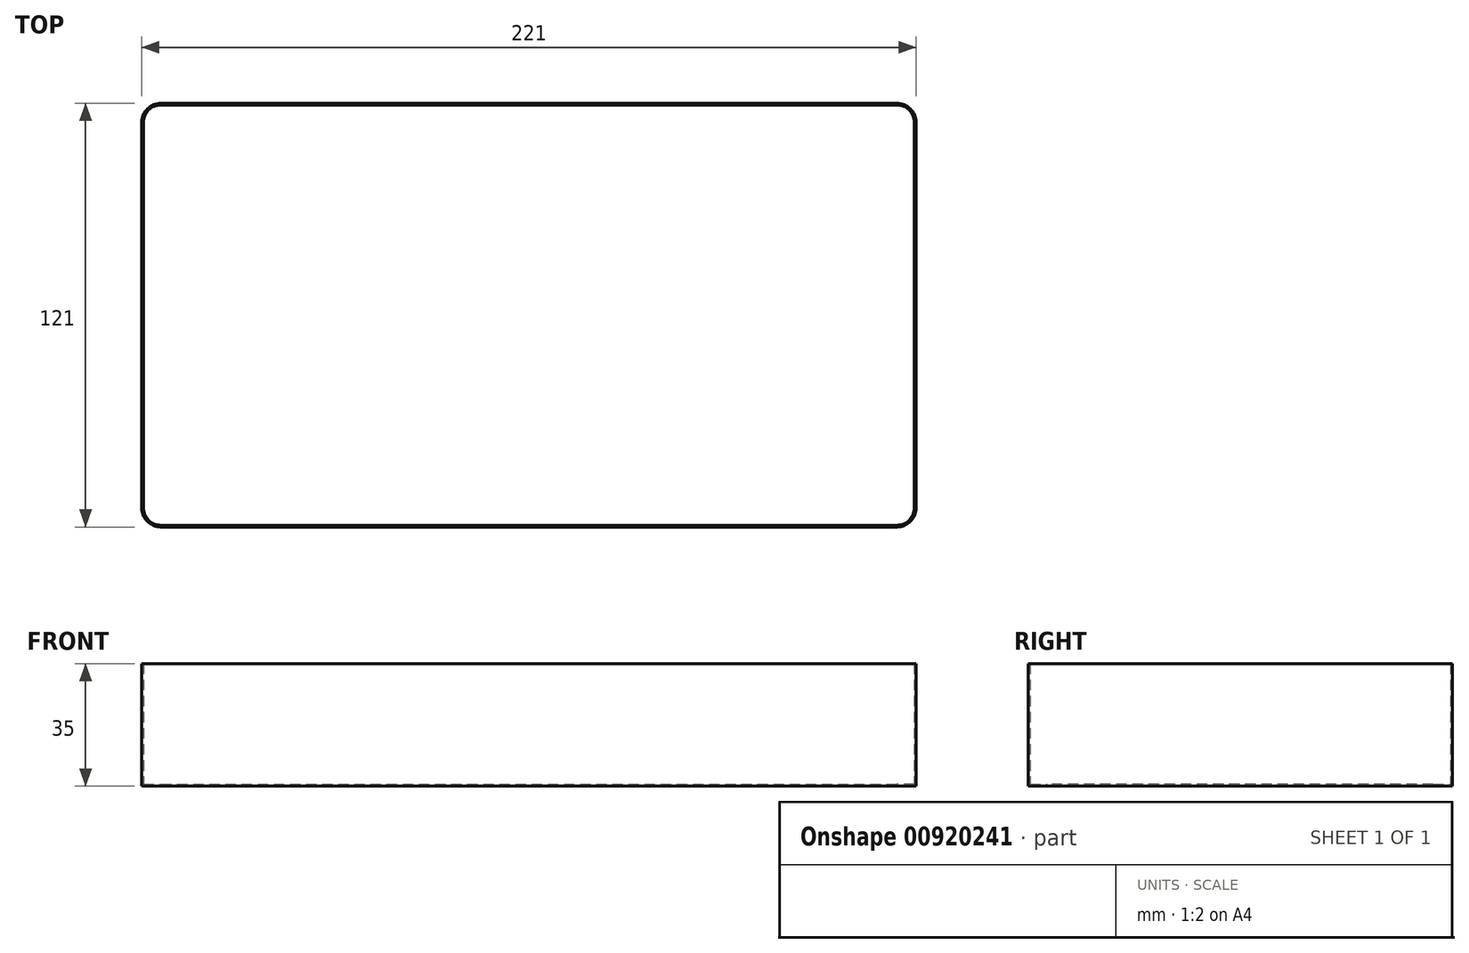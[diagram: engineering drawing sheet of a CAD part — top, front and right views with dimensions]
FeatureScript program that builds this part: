
annotation { "Feature Type Name" : "Feature", "Feature Type Description" : "" }
export const myFeature = defineFeature(function(context is Context, id is Id, definition is map)
    precondition{}
    {
        {
            var Q0;
            Q0=qCreatedBy(makeId("Top.planeOp"),FACE);
            var sketch = newSketch(context, id + "F0", { "sketchPlane" : qUnion([Q0])});
            skLineSegment(sketch, "E0.bottom", {"start": v(105, -60) * mm, "end": v(-105, -60) * mm});
            skLineSegment(sketch, "E0.top", {"start": v(105, 60) * mm, "end": v(-105, 60) * mm});
            skLineSegment(sketch, "E0.left", {"start": v(110, -55) * mm, "end": v(110, 55) * mm});
            skLineSegment(sketch, "E0.right", {"start": v(-110, -55) * mm, "end": v(-110, 55) * mm});
            skPoint(sketch, "E0.middle", {"position": v(0, 0) * mm});
            skPoint(sketch, "E1.visualSharp", {"position": v(-110, 60) * mm});
            skArc(sketch, "E1.filletArc", {"start": v(-105, 60) * mm, "mid": v(-108.54, 58.54) * mm, "end": v(-110, 55) * mm});
            skPoint(sketch, "E2.visualSharp", {"position": v(110, 60) * mm});
            skArc(sketch, "E2.filletArc", {"start": v(110, 55) * mm, "mid": v(108.54, 58.54) * mm, "end": v(105, 60) * mm});
            skPoint(sketch, "E3.visualSharp", {"position": v(110, -60) * mm});
            skArc(sketch, "E3.filletArc", {"start": v(105, -60) * mm, "mid": v(108.54, -58.54) * mm, "end": v(110, -55) * mm});
            skPoint(sketch, "E4.visualSharp", {"position": v(-110, -60) * mm});
            skArc(sketch, "E4.filletArc", {"start": v(-110, -55) * mm, "mid": v(-108.54, -58.54) * mm, "end": v(-105, -60) * mm});
            skArc(sketch, "E5.0", {"start": v(110.5, 55) * mm, "mid": v(108.89, 58.89) * mm, "end": v(105, 60.5) * mm});
            skLineSegment(sketch, "E5.1", {"start": v(110.5, -55) * mm, "end": v(110.5, 55) * mm});
            skLineSegment(sketch, "E5.2", {"start": v(105, 60.5) * mm, "end": v(-105, 60.5) * mm});
            skArc(sketch, "E5.3", {"start": v(105, -60.5) * mm, "mid": v(108.89, -58.89) * mm, "end": v(110.5, -55) * mm});
            skArc(sketch, "E5.4", {"start": v(-105, 60.5) * mm, "mid": v(-108.89, 58.89) * mm, "end": v(-110.5, 55) * mm});
            skLineSegment(sketch, "E5.5", {"start": v(-110.5, -55) * mm, "end": v(-110.5, 55) * mm});
            skArc(sketch, "E5.6", {"start": v(-110.5, -55) * mm, "mid": v(-108.89, -58.89) * mm, "end": v(-105, -60.5) * mm});
            skLineSegment(sketch, "E5.7", {"start": v(105, -60.5) * mm, "end": v(-105, -60.5) * mm});
            skSolve(sketch);
        }
        {
            var Q0;
            Q0=makeQuery(id+"F0.imprint","IMPRINT",FACE,{"disambiguationData":[TD([[makeQuery(id+"F0.imprint","IMPRINT",EDGE,{"derivedFrom":sQuery(id+"F0.wireOp",EDGE,"E0.bottom")}),-1.0]])]});
            var Q1;
            Q1=makeQuery(id+"F0.imprint","IMPRINT",FACE,{"disambiguationData":[TD([[makeQuery(id+"F0.imprint","IMPRINT",EDGE,{"derivedFrom":sQuery(id+"F0.wireOp",EDGE,"E0.bottom")}),1.0]])]});
            extrude(context, id + "F1", {"entities" : qUnion([Q0, Q1]), "depth" : 0.5 * mm, "offsetDistance" : 25 * mm});
        }
        {
            var Q0;
            Q0=makeQuery(id+"F0.imprint","IMPRINT",FACE,{"disambiguationData":[TD([[makeQuery(id+"F0.imprint","IMPRINT",EDGE,{"derivedFrom":sQuery(id+"F0.wireOp",EDGE,"E0.bottom")}),1.0]])]});
            extrude(context, id + "F2", {"entities" : qUnion([Q0]), "operationType" : NewBodyOperationType.ADD, "depth" : 35 * mm, "offsetDistance" : 25 * mm});
        }
    });
